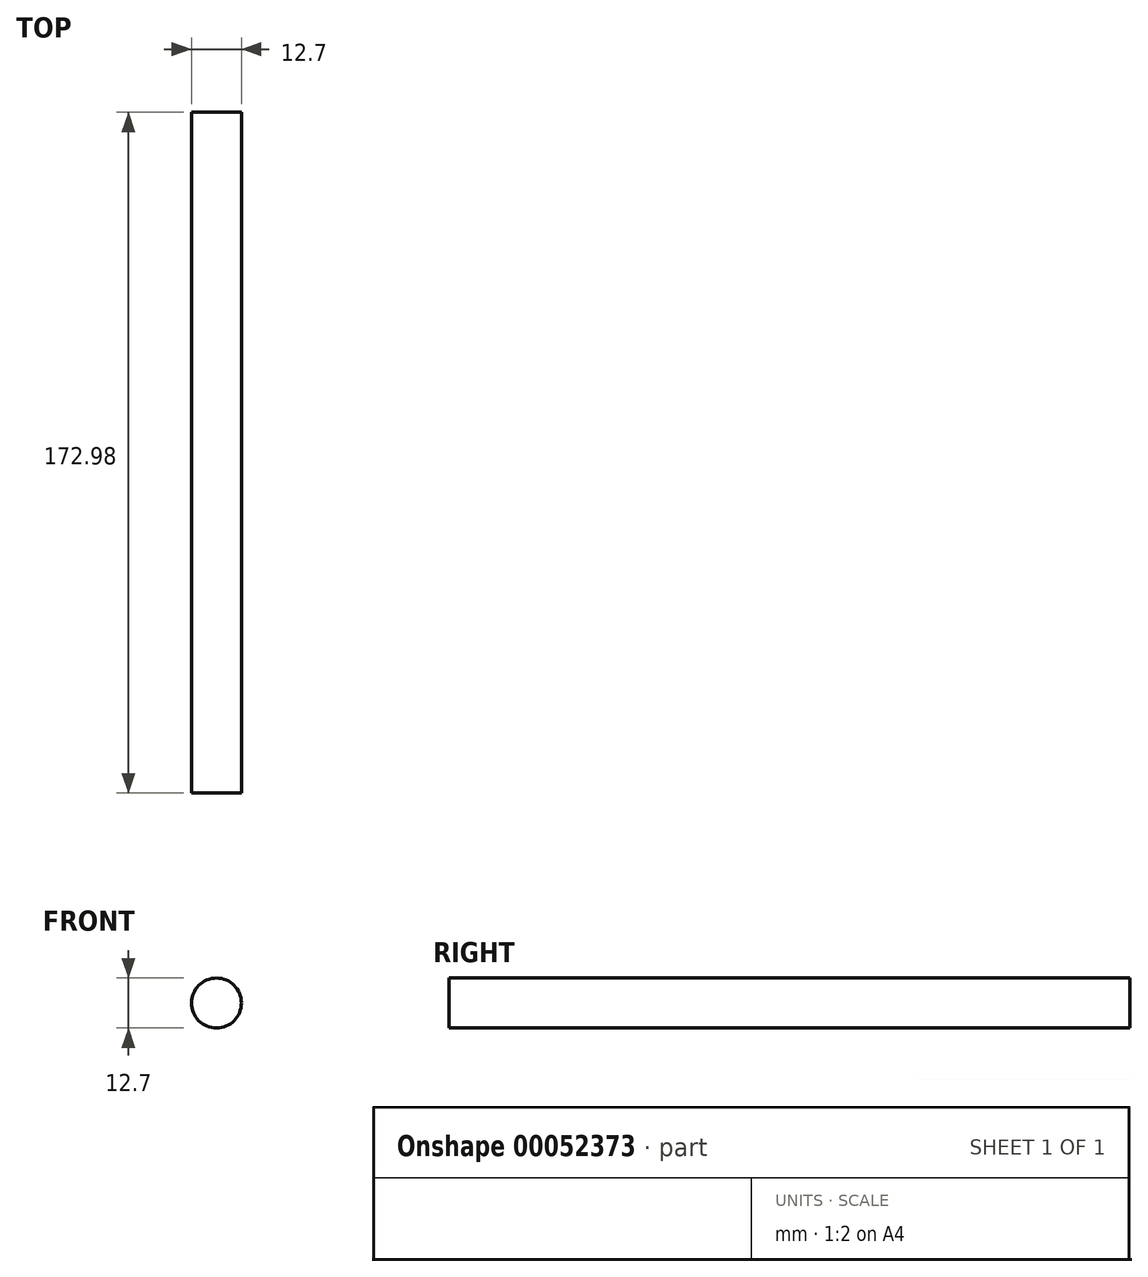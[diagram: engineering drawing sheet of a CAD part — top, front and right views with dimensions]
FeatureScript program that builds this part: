
annotation { "Feature Type Name" : "Feature", "Feature Type Description" : "" }
export const myFeature = defineFeature(function(context is Context, id is Id, definition is map)
    precondition{}
    {
        {
            var Q0;
            Q0=qCreatedBy(makeId("Front.planeOp"),FACE);
            var sketch = newSketch(context, id + "F0", { "sketchPlane" : qUnion([Q0])});
            skCircle(sketch, "E0", {"center": v(0, 0) * mm, "radius": 6.35 * mm});
            skSolve(sketch);
        }
        {
            var Q0;
            Q0 = qSketchRegion(id + "F0", true);
            extrude(context, id + "F1", {"entities" : qUnion([Q0]), "depth" : 172.97 * mm, "symmetric" : true});
        }
    });
